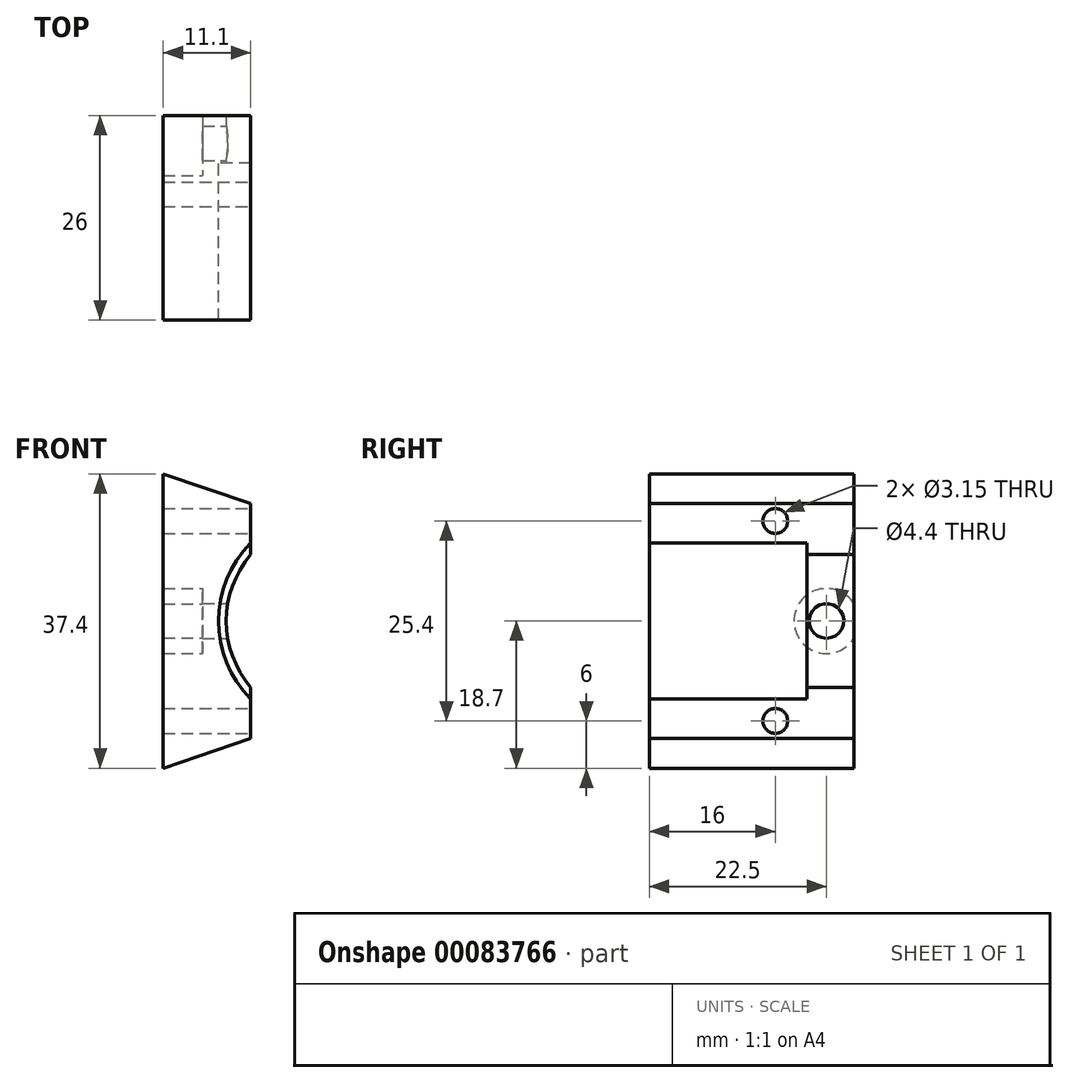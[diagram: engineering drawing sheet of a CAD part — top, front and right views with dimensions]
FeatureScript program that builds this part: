
annotation { "Feature Type Name" : "Feature", "Feature Type Description" : "" }
export const myFeature = defineFeature(function(context is Context, id is Id, definition is map)
    precondition{}
    {
        {
            assignVariable(context, id + "F0", {"name" : "height", "anyValue" : 20 * mm});
        }
        {
            var Q0;
            Q0=qCreatedBy(makeId("Front.planeOp"),FACE);
            var sketch = newSketch(context, id + "F1", { "sketchPlane" : qUnion([Q0])});
            skArc(sketch, "E0", {"start": v(-9.9, 9.9) * mm, "mid": v(-14, 0) * mm, "end": v(-9.9, -9.9) * mm});
            skLineSegment(sketch, "E1", {"start": v(0, 0) * mm, "end": v(-9.9, 9.9) * mm, "construction": true});
            skLineSegment(sketch, "E2", {"start": v(-9.9, -9.9) * mm, "end": v(0, 0) * mm, "construction": true});
            skLineSegment(sketch, "E3", {"start": v(-9.9, 9.9) * mm, "end": v(-9.9, -9.9) * mm, "construction": true});
            skLineSegment(sketch, "E4", {"start": v(-21, 18.7) * mm, "end": v(-21, -18.7) * mm});
            skPoint(sketch, "E5", {"position": v(-21, 0) * mm});
            skLineSegment(sketch, "E6", {"start": v(-9.9, 9.9) * mm, "end": v(-9.9, 14.9) * mm});
            skLineSegment(sketch, "E7", {"start": v(-21, 18.7) * mm, "end": v(-9.9, 14.9) * mm});
            skLineSegment(sketch, "E8", {"start": v(-9.9, -9.9) * mm, "end": v(-9.9, -14.9) * mm});
            skLineSegment(sketch, "E9", {"start": v(-9.9, -14.9) * mm, "end": v(-21, -18.7) * mm});
            skSolve(sketch);
        }
        {
            var Q0;
            Q0 = qSketchRegion(id + "F1", true);
            extrude(context, id + "F2", {"entities" : qUnion([Q0]), "depth" : getVariable(context, 'height')});
        }
        {
            var Q0;
            Q0=makeQuery(id+"F2.opExtrude","CAP_FACE",FACE,{"disambiguationData":[OSD([sQuery(id+"F1.wireOp",EDGE,"E0"),sQuery(id+"F1.wireOp",EDGE,"E4"),sQuery(id+"F1.wireOp",EDGE,"E6"),sQuery(id+"F1.wireOp",EDGE,"E7"),sQuery(id+"F1.wireOp",EDGE,"E8"),sQuery(id+"F1.wireOp",EDGE,"E9")])],"isStart":true});
            var sketch = newSketch(context, id + "F3", { "sketchPlane" : qUnion([Q0])});
            skArc(sketch, "E10.0", {"start": v(9.9, 8.43) * mm, "mid": v(13, 0) * mm, "end": v(9.9, -8.43) * mm});
            skLineSegment(sketch, "E11.0", {"start": v(21, 18.7) * mm, "end": v(9.9, 14.9) * mm});
            skLineSegment(sketch, "E12.0", {"start": v(21, 18.7) * mm, "end": v(21, -18.7) * mm});
            skLineSegment(sketch, "E13.0", {"start": v(9.9, -14.9) * mm, "end": v(21, -18.7) * mm});
            skLineSegment(sketch, "E14", {"start": v(9.9, 8.43) * mm, "end": v(9.9, 14.9) * mm});
            skLineSegment(sketch, "E15", {"start": v(9.9, -14.9) * mm, "end": v(9.9, -8.43) * mm});
            skSolve(sketch);
        }
        {
            var Q0;
            Q0 = qSketchRegion(id + "F3", true);
            extrude(context, id + "F4", {"entities" : qUnion([Q0]), "operationType" : NewBodyOperationType.ADD, "depth" : 6 * mm});
        }
        {
            var Q0;
            Q0=makeQuery(id+"F4.boolean.opBoolean","MERGE",FACE,{"derivedFrom":[makeQuery(id+"F2.opExtrude","SWEPT_FACE",FACE,{"disambiguationData":[OSD([sQuery(id+"F1.wireOp",EDGE,"E4")])]}),makeQuery(id+"F4.opExtrude","SWEPT_FACE",FACE,{"disambiguationData":[OSD([sQuery(id+"F3.wireOp",EDGE,"E12.0")])]})]});
            var sketch = newSketch(context, id + "F5", { "sketchPlane" : qUnion([Q0])});
            skLineSegment(sketch, "E16", {"start": v(20, -12.7) * mm, "end": v(-6, -12.7) * mm, "construction": true});
            skLineSegment(sketch, "E17", {"start": v(20, 12.7) * mm, "end": v(-6, 12.7) * mm, "construction": true});
            skPoint(sketch, "E18", {"position": v(4, 12.7) * mm});
            skPoint(sketch, "E19", {"position": v(4, -12.7) * mm});
            skLineSegment(sketch, "E20", {"start": v(-6, 0) * mm, "end": v(-6, -12.7) * mm, "construction": true});
            skLineSegment(sketch, "E21", {"start": v(-6, 0) * mm, "end": v(-6, 12.7) * mm, "construction": true});
            skLineSegment(sketch, "E22.0", {"start": v(0, 8.43) * mm, "end": v(0, -8.43) * mm, "construction": true});
            skPoint(sketch, "E23", {"position": v(-2.5, 0) * mm});
            skSolve(sketch);
        }
        {
            var Q0;
            Q0=sQuery(id+"F5.wireOp",VERTEX,"E18");
            var Q1;
            Q1=sQuery(id+"F5.wireOp",VERTEX,"E19");
            var Q2;
            Q2=makeQuery(id+"F2.opExtrude","SWEPT_BODY",BODY,{"disambiguationData":[OSD([sQuery(id+"F1.wireOp",EDGE,"E0"),sQuery(id+"F1.wireOp",EDGE,"E4"),sQuery(id+"F1.wireOp",EDGE,"E6"),sQuery(id+"F1.wireOp",EDGE,"E7"),sQuery(id+"F1.wireOp",EDGE,"E8"),sQuery(id+"F1.wireOp",EDGE,"E9")])]});
            hole(context, id + "F6", {"style" : HoleStyle.SIMPLE, "endStyle" : HoleEndStyle.THROUGH, "standardTappedOrClearance" : lookupTablePath({ "standard" : "ISO", "fit" : "Close", "size" : "M3", "type" : "Clearance" }), "standardBlindInLast" : lookupTablePath({ "fit" : "Close", "standard" : "ISO", "size" : "M3", "type" : "Clearance" }), "holeDiameter" : 3.15 * mm, "startFromSketch" : true, "locations" : qUnion([Q0, Q1]), "scope" : qUnion([Q2]), "isTappedThrough" : true});
        }
        {
            var Q0;
            Q0=sQuery(id+"F5.wireOp",VERTEX,"E23");
            var Q1;
            Q1=makeQuery(id+"F2.opExtrude","SWEPT_BODY",BODY,{"disambiguationData":[OSD([sQuery(id+"F1.wireOp",EDGE,"E0"),sQuery(id+"F1.wireOp",EDGE,"E4"),sQuery(id+"F1.wireOp",EDGE,"E6"),sQuery(id+"F1.wireOp",EDGE,"E7"),sQuery(id+"F1.wireOp",EDGE,"E8"),sQuery(id+"F1.wireOp",EDGE,"E9")])]});
            hole(context, id + "F7", {"style" : HoleStyle.C_BORE, "endStyle" : HoleEndStyle.THROUGH, "holeDiameter" : 4.4 * mm, "cBoreDiameter" : 8.25 * mm, "cBoreDepth" : 5 * mm, "startFromSketch" : true, "locations" : qUnion([Q0]), "scope" : qUnion([Q1]), "isTappedThrough" : true});
        }
    });
